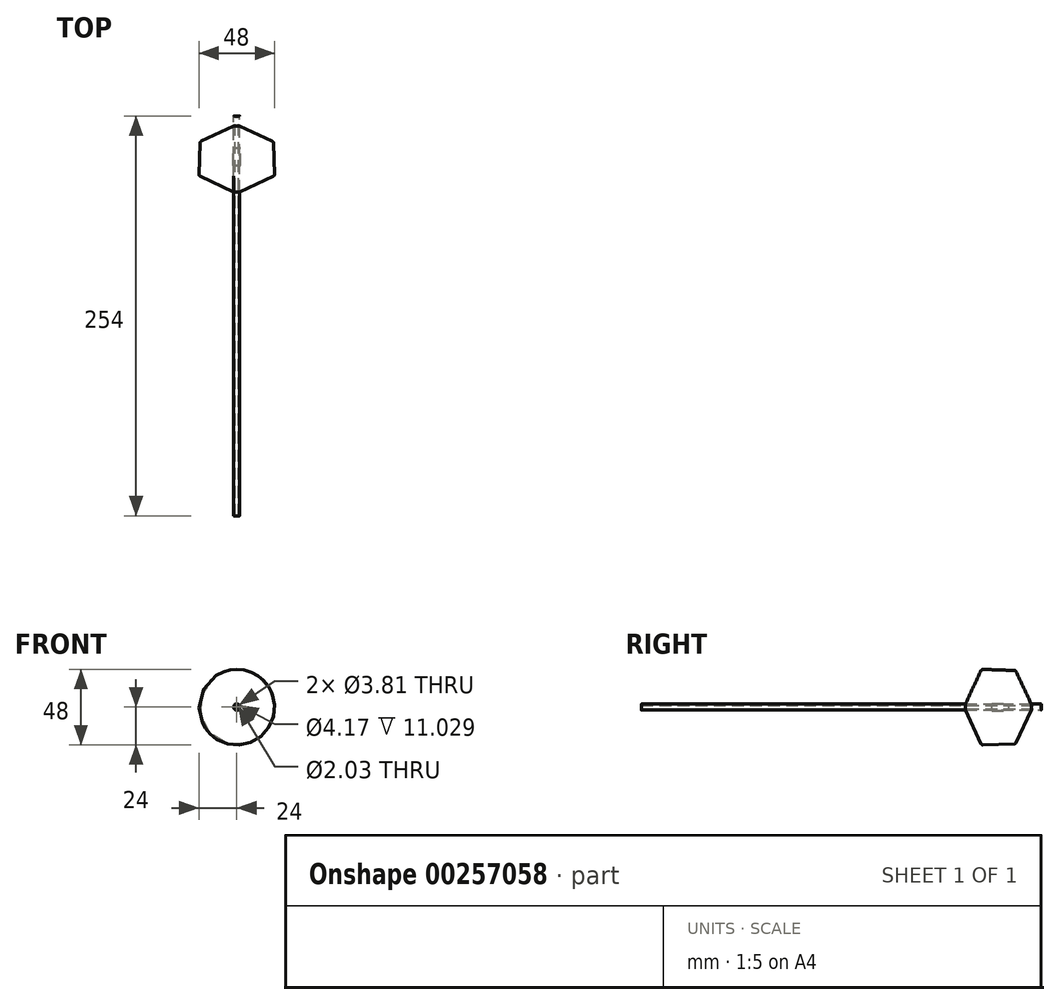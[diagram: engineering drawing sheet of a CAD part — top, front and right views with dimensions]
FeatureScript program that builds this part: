
annotation { "Feature Type Name" : "Feature", "Feature Type Description" : "" }
export const myFeature = defineFeature(function(context is Context, id is Id, definition is map)
    precondition{}
    {
        {
            var Q0;
            Q0=qCreatedBy(makeId("Front.planeOp"),FACE);
            var sketch = newSketch(context, id + "F0", { "sketchPlane" : qUnion([Q0])});
            skCircle(sketch, "E0", {"center": v(0, 0) * mm, "radius": 1.02 * mm});
            skCircle(sketch, "E1", {"center": v(0, 0) * mm, "radius": 1.9 * mm});
            skSolve(sketch);
        }
        {
            var Q0;
            Q0=makeQuery(id+"F0.imprint","IMPRINT",FACE,{"disambiguationData":[TD([[makeQuery(id+"F0.imprint","IMPRINT",EDGE,{"derivedFrom":sQuery(id+"F0.wireOp",EDGE,"E0")}),-1.0]])]});
            extrude(context, id + "F1", {"entities" : qUnion([Q0]), "depth" : 254 * mm});
        }
        {
            var Q0;
            Q0=makeQuery(id+"F1.opExtrude","CAP_EDGE",EDGE,{"disambiguationData":[OSD([sQuery(id+"F0.wireOp",EDGE,"E0")])],"isStart":true});
            chamfer(context, id + "F2", {"entities" : qUnion([Q0]), "width" : 0.56 * mm, "tangentPropagation" : true});
        }
        {
            var Q0;
            Q0=makeQuery(id+"F1.opExtrude","CAP_EDGE",EDGE,{"disambiguationData":[OSD([sQuery(id+"F0.wireOp",EDGE,"E1")])],"isStart":true});
            fillet(context, id + "F3", {"entities" : qUnion([Q0]), "radius" : 0.13 * mm, "tangentPropagation" : true, "allowEdgeOverflow" : false});
        }
        {
            var Q0;
            Q0=makeQuery(id+"F1.opExtrude","CAP_EDGE",EDGE,{"disambiguationData":[OSD([sQuery(id+"F0.wireOp",EDGE,"E1")])],"isStart":false});
            fillet(context, id + "F4", {"entities" : qUnion([Q0]), "radius" : 0.13 * mm, "tangentPropagation" : true, "allowEdgeOverflow" : false});
        }
        {
            var Q0;
            Q0=qCreatedBy(makeId("Right.planeOp"),FACE);
            var sketch = newSketch(context, id + "F5", { "sketchPlane" : qUnion([Q0])});
            skLineSegment(sketch, "E2", {"start": v(0, 0) * mm, "end": v(-318.3, 0) * mm, "construction": true});
            skSolve(sketch);
        }
        {
            var Q0;
            Q0=qCreatedBy(makeId("Right.planeOp"),FACE);
            var sketch = newSketch(context, id + "F6", { "sketchPlane" : qUnion([Q0])});
            skLineSegment(sketch, "E3.0", {"start": v(-253.87, 0) * mm, "end": v(-253.87, -1.9) * mm, "construction": true});
            skLineSegment(sketch, "E4", {"start": v(-48.25, 1.9) * mm, "end": v(-48.2, 1.9) * mm});
            skLineSegment(sketch, "E5", {"start": v(-48.25, 1.9) * mm, "end": v(-38.29, 23.27) * mm});
            skLineSegment(sketch, "E6", {"start": v(-37.1, 24) * mm, "end": v(-17.1, 23.3) * mm});
            skLineSegment(sketch, "E7.0", {"start": v(0, 0) * mm, "end": v(-318.3, 0) * mm, "construction": true});
            skLineSegment(sketch, "E8", {"start": v(-48.2, 1.9) * mm, "end": v(-38.26, 23.22) * mm});
            skLineSegment(sketch, "E9", {"start": v(-37.06, 23.95) * mm, "end": v(-30.48, 23.72) * mm});
            skPoint(sketch, "E10.orphan", {"position": v(-253.87, 1.9) * mm});
            skPoint(sketch, "E11.orphan", {"position": v(-37.93, 1.9) * mm});
            skPoint(sketch, "E12.visualSharp", {"position": v(-37.93, 24.03) * mm});
            skArc(sketch, "E12.filletArc", {"start": v(-37.1, 24) * mm, "mid": v(-37.8, 23.81) * mm, "end": v(-38.29, 23.27) * mm});
            skPoint(sketch, "E13.visualSharp", {"position": v(-37.9, 23.98) * mm});
            skArc(sketch, "E13.filletArc", {"start": v(-37.06, 23.95) * mm, "mid": v(-37.77, 23.76) * mm, "end": v(-38.26, 23.22) * mm});
            skLineSegment(sketch, "E14", {"start": v(-6.4, 1.9) * mm, "end": v(-6.35, 1.9) * mm});
            skLineSegment(sketch, "E15", {"start": v(-15.99, 22.57) * mm, "end": v(-6.35, 1.9) * mm});
            skLineSegment(sketch, "E16", {"start": v(-16.02, 22.54) * mm, "end": v(-6.4, 1.9) * mm});
            skPoint(sketch, "E17.visualSharp", {"position": v(-16.34, 23.22) * mm});
            skArc(sketch, "E17.filletArc", {"start": v(-16.02, 22.54) * mm, "mid": v(-16.46, 23.05) * mm, "end": v(-17.1, 23.25) * mm});
            skPoint(sketch, "E18.visualSharp", {"position": v(-16.31, 23.27) * mm});
            skArc(sketch, "E18.filletArc", {"start": v(-15.99, 22.57) * mm, "mid": v(-16.44, 23.1) * mm, "end": v(-17.1, 23.3) * mm});
            skLineSegment(sketch, "E19", {"start": v(-30.46, 23.72) * mm, "end": v(-30.45, 23.74) * mm});
            skLineSegment(sketch, "E20", {"start": v(-30.43, 23.74) * mm, "end": v(-23.77, 23.5) * mm});
            skLineSegment(sketch, "E21", {"start": v(-23.75, 23.5) * mm, "end": v(-23.74, 23.5) * mm});
            skLineSegment(sketch, "E22.trimOffspring", {"start": v(-23.72, 23.48) * mm, "end": v(-17.1, 23.25) * mm});
            skPoint(sketch, "E23.visualSharp", {"position": v(-30.47, 23.72) * mm});
            skArc(sketch, "E23.filletArc", {"start": v(-30.48, 23.72) * mm, "mid": v(-30.47, 23.72) * mm, "end": v(-30.46, 23.72) * mm});
            skPoint(sketch, "E24.visualSharp", {"position": v(-30.44, 23.74) * mm});
            skArc(sketch, "E24.filletArc", {"start": v(-30.43, 23.74) * mm, "mid": v(-30.44, 23.74) * mm, "end": v(-30.45, 23.74) * mm});
            skPoint(sketch, "E25.visualSharp", {"position": v(-23.76, 23.5) * mm});
            skArc(sketch, "E25.filletArc", {"start": v(-23.75, 23.5) * mm, "mid": v(-23.76, 23.5) * mm, "end": v(-23.77, 23.5) * mm});
            skPoint(sketch, "E26.visualSharp", {"position": v(-23.73, 23.48) * mm});
            skArc(sketch, "E26.filletArc", {"start": v(-23.74, 23.5) * mm, "mid": v(-23.73, 23.48) * mm, "end": v(-23.72, 23.48) * mm});
            skSolve(sketch);
        }
        {
            var Q0;
            Q0=qSketchRegion(id+"F6",true);
            var Q1;
            Q1=sQuery(id+"F6.wireOp",EDGE,"E7.0");
            revolve(context, id + "F7", {"entities" : qUnion([Q0]), "axis" : qUnion([Q1]), "revolveType" : RevolveType.FULL});
        }
        {
            var Q0;
            Q0=qCreatedBy(makeId("Front.planeOp"),FACE);
            cPlane(context, id + "F8", {"entities" : qUnion([Q0]), "cplaneType" : CPlaneType.OFFSET, "offset" : 20.42 * mm, "width" : 152.4 * mm, "height" : 152.4 * mm});
        }
        {
            var Q0;
            Q0=qCreatedBy(makeId("Front.planeOp"),FACE);
            cPlane(context, id + "F9", {"entities" : qUnion([Q0]), "cplaneType" : CPlaneType.OFFSET, "offset" : 31.45 * mm, "width" : 152.4 * mm, "height" : 152.4 * mm});
        }
        {
            var Q0;
            Q0=qCreatedBy(id+"F9.planeOp",FACE);
            var sketch = newSketch(context, id + "F10", { "sketchPlane" : qUnion([Q0])});
            skCircle(sketch, "E27.0", {"center": v(0, 0) * mm, "radius": 24 * mm, "construction": true});
            skArc(sketch, "E28", {"start": v(22.85, 7.33) * mm, "mid": v(0, -24) * mm, "end": v(-22.85, 7.33) * mm});
            skLineSegment(sketch, "E29", {"start": v(0, 18.59) * mm, "end": v(0, -14.82) * mm, "construction": true});
            skLineSegment(sketch, "E30", {"start": v(-18.7, 0) * mm, "end": v(23.1, 0) * mm, "construction": true});
            skArc(sketch, "E31.MirrorCS", {"start": v(22.85, -7.33) * mm, "mid": v(0, 24) * mm, "end": v(-22.85, -7.33) * mm});
            skArc(sketch, "E32", {"start": v(22.6, 8.05) * mm, "mid": v(-24, 0) * mm, "end": v(22.6, -8.05) * mm});
            skArc(sketch, "E33.MirrorCS", {"start": v(-22.6, 8.05) * mm, "mid": v(24, 0) * mm, "end": v(-22.6, -8.05) * mm});
            skSolve(sketch);
        }
        {
            var Q0;
            Q0=qCreatedBy(id+"F8.planeOp",FACE);
            var sketch = newSketch(context, id + "F11", { "sketchPlane" : qUnion([Q0])});
            skCircle(sketch, "E34.0", {"center": v(0, 0) * mm, "radius": 24 * mm, "construction": true});
            skArc(sketch, "E35", {"start": v(-22.85, 7.33) * mm, "mid": v(0, 24) * mm, "end": v(22.85, 7.33) * mm});
            skLineSegment(sketch, "E36", {"start": v(0, 18.32) * mm, "end": v(0, -15.1) * mm, "construction": true});
            skLineSegment(sketch, "E37", {"start": v(-19.02, 0) * mm, "end": v(22.78, 0) * mm, "construction": true});
            skArc(sketch, "E38.MirrorCS", {"start": v(-22.85, -7.33) * mm, "mid": v(0, -24) * mm, "end": v(22.85, -7.33) * mm});
            skArc(sketch, "E39", {"start": v(-23.08, 6.6) * mm, "mid": v(-24, 0) * mm, "end": v(-23.08, -6.6) * mm});
            skArc(sketch, "E40.MirrorCS", {"start": v(23.08, 6.6) * mm, "mid": v(24, 0) * mm, "end": v(23.08, -6.6) * mm});
            skSolve(sketch);
        }
        {
            var Q0;
            Q0=qCreatedBy(id+"F8.planeOp",FACE);
            var sketch = newSketch(context, id + "F12", { "sketchPlane" : qUnion([Q0])});
            skCircle(sketch, "E41", {"center": v(0, 0) * mm, "radius": 2.47 * mm});
            skCircle(sketch, "E42", {"center": v(0, 0) * mm, "radius": 2.08 * mm});
            skSolve(sketch);
        }
        {
            var Q0;
            Q0=qSketchRegion(id+"F12",true);
            var Q1;
            Q1=qCreatedBy(id+"F9.planeOp",FACE);
            extrude(context, id + "F13", {"entities" : qUnion([Q0]), "operationType" : NewBodyOperationType.ADD, "endBound" : BoundingType.UP_TO_SURFACE, "endBoundEntityFace" : qUnion([Q1]), "depth" : 25.4 * mm});
        }
    });
